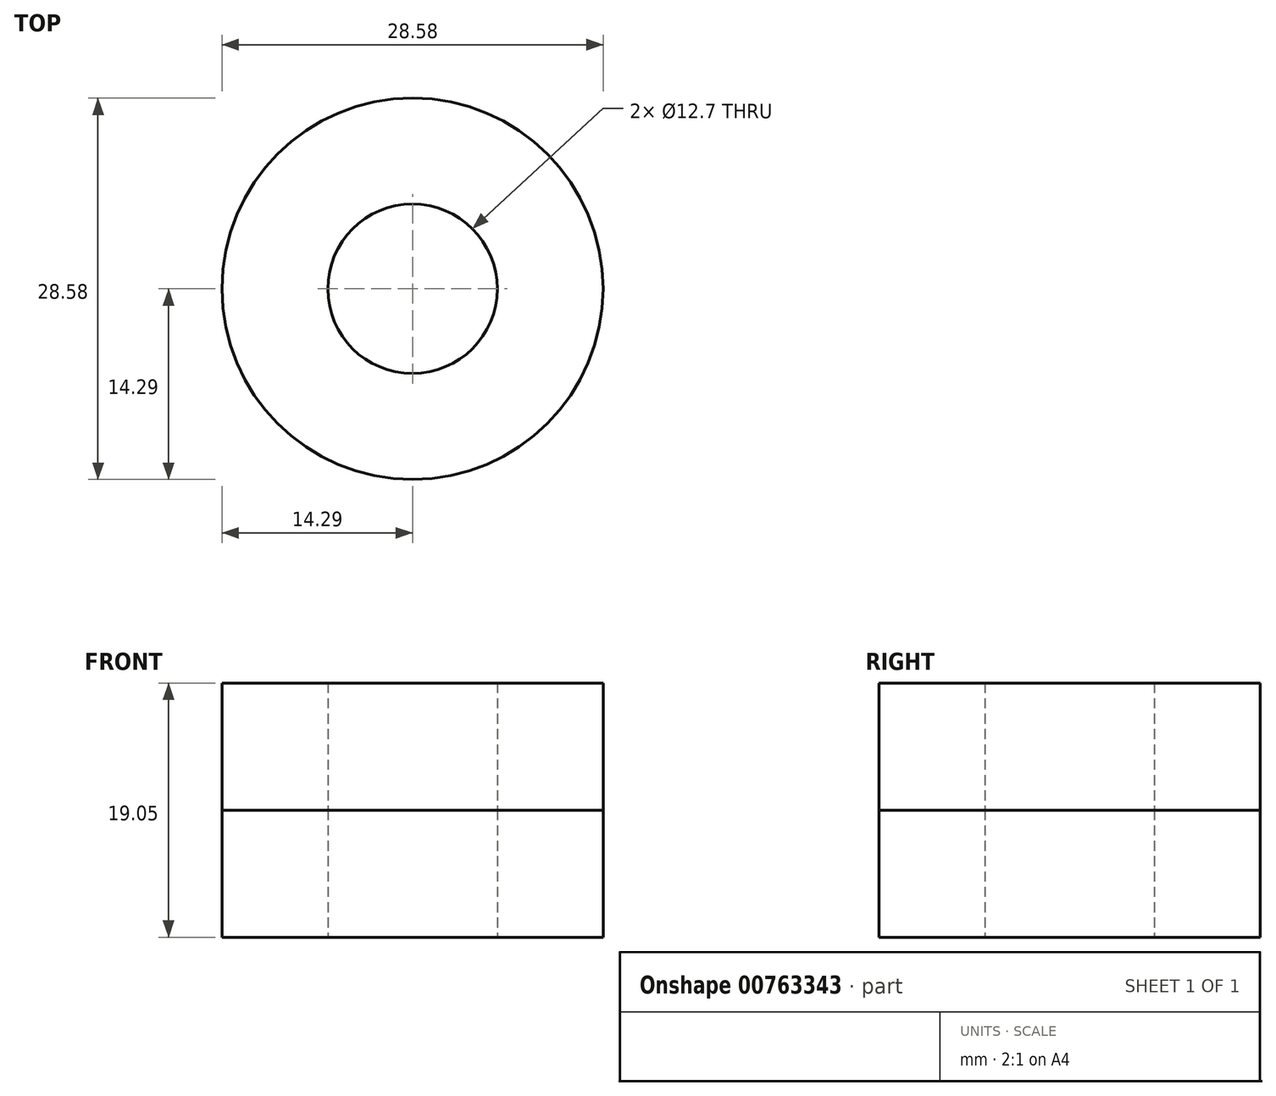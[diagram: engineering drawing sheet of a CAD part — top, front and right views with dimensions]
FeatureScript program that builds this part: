
annotation { "Feature Type Name" : "Feature", "Feature Type Description" : "" }
export const myFeature = defineFeature(function(context is Context, id is Id, definition is map)
    precondition{}
    {
        {
            var Q0;
            Q0=qCreatedBy(makeId("Top.planeOp"),FACE);
            var sketch = newSketch(context, id + "F0", { "sketchPlane" : qUnion([Q0])});
            skCircle(sketch, "E0", {"center": v(0, 0) * mm, "radius": 6.35 * mm});
            skCircle(sketch, "E1", {"center": v(0, 0) * mm, "radius": 14.29 * mm});
            skSolve(sketch);
        }
        {
            var Q0;
            Q0=makeQuery(id+"F0.imprint","IMPRINT",FACE,{"disambiguationData":[TD([[makeQuery(id+"F0.imprint","IMPRINT",EDGE,{"derivedFrom":sQuery(id+"F0.wireOp",EDGE,"E0")}),-1.0]])]});
            extrude(context, id + "F1", {"entities" : qUnion([Q0]), "depth" : 9.52 * mm, "offsetDistance" : 25.4 * mm});
        }
        {
            var Q0;
            Q0=makeQuery(id+"F1.opExtrude","CAP_FACE",FACE,{"disambiguationData":[OSD([sQuery(id+"F0.wireOp",EDGE,"E0"),sQuery(id+"F0.wireOp",EDGE,"E1")])],"isStart":false});
            var sketch = newSketch(context, id + "F2", { "sketchPlane" : qUnion([Q0])});
            skCircle(sketch, "E2.0", {"center": v(0, 0) * mm, "radius": 14.29 * mm});
            skSolve(sketch);
        }
        {
            var Q0;
            Q0=makeQuery(id+"F2.imprint","IMPRINT",FACE,{"disambiguationData":[TD([[makeQuery(id+"F2.imprint","IMPRINT",EDGE,{"derivedFrom":sQuery(id+"F2.wireOp",EDGE,"E2.0")}),1.0]])]});
            extrude(context, id + "F3", {"entities" : qUnion([Q0]), "depth" : 9.52 * mm, "offsetDistance" : 25.4 * mm});
        }
    });
